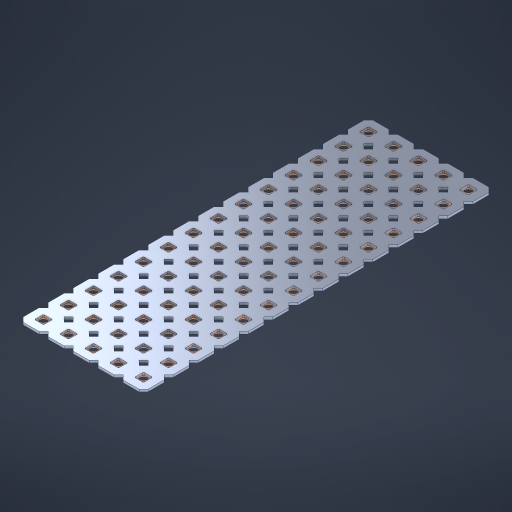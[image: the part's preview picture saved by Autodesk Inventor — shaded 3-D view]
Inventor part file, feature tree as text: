
AUTODESK INVENTOR PART (.ipt)
format: ipt  version: 2023 (Build 270158000, 158)  size: 1,072,128 bytes
history: native  units: in
note: dims shown in document units (in); Inventor stores cm internally (conversion verified against a paired STEP export)
features: other x71, extrude x69, sketch x2, pattern_linear x1
ambient origin geometry x8: Origin, YZ Plane, XZ Plane, XY Plane, X Axis, Y Axis, Z Axis, Center Point
bodies: Solid1 (feature_tree), Body (feature_tree)
feature tree (143):
  pattern_linear  "Rectangular Pattern1"  Spacing1=0.09in  [1 undecoded]
  sketch  "Sketch1"  dims[d1=0.5in]
  sketch  "Sketch2"  dims[d2=0.182in d3=0.09in d4=0.09in d5=0.09in d6=0.09in d7=0.09in d8=0.09in d9=0.09in d10=0.09in d11=0.02in d13=0.0in d14=0.172in d15=0.0625in d16=0.0in d19=0.5in d22=0.5in]
  other  "Srf1"
  other  "Srf126"
  other  "Srf127"
  other  "Srf128"
  other  "Srf129"
  other  "Srf130"
  other  "Srf131"
  other  "Srf250"
  other  "Srf251"
  other  "Srf252"
  other  "Srf253"
  other  "Srf254"
  other  "Srf255"
  other  "Srf256"
  other  "Srf268"
  other  "Srf269"
  other  "Srf270"
  other  "Srf271"
  other  "Srf272"
  other  "Srf273"
  other  "Srf274"
  other  "Srf275"
  other  "Srf276"
  other  "Srf277"
  other  "Srf278"
  other  "Srf279"
  other  "Srf280"
  other  "Srf281"
  other  "Srf293"
  other  "Srf294"
  other  "Srf295"
  other  "Srf296"
  other  "Srf297"
  other  "Srf298"
  other  "Srf299"
  other  "Srf300"
  other  "Srf301"
  other  "Srf302"
  other  "Srf303"
  other  "Srf304"
  other  "Srf305"
  other  "Srf306"
  other  "Srf318"
  other  "Srf319"
  other  "Srf320"
  other  "Srf321"
  other  "Srf322"
  other  "Srf323"
  other  "Srf324"
  other  "Srf325"
  other  "Srf326"
  other  "Srf327"
  other  "Srf328"
  other  "Srf329"
  other  "Srf330"
  other  "Srf331"
  other  "Srf343"
  other  "Srf344"
  other  "Srf345"
  other  "Srf346"
  other  "Srf347"
  other  "Srf348"
  other  "Srf349"
  other  "Srf350"
  other  "Srf351"
  other  "Srf352"
  other  "Srf353"
  other  "Srf354"
  other  "Srf355"
  other  "Srf356"
  other  "Circle"
  extrude  "ExtrusionSrf126"  Depth=0.09in
  extrude  "ExtrusionSrf127"  Depth=0.09in
  extrude  "ExtrusionSrf128"  Depth=0.09in
  extrude  "ExtrusionSrf129"  Depth=0.09in
  extrude  "ExtrusionSrf130"  Depth=0.09in
  extrude  "ExtrusionSrf131"  Depth=0.09in
  extrude  "ExtrusionSrf250"  Depth=0.09in
  extrude  "ExtrusionSrf251"  Depth=0.02in
  extrude  "ExtrusionSrf252"  TaperAngle=0.0deg  [1 undecoded]
  extrude  "ExtrusionSrf253"  Depth=0.5in
  extrude  "ExtrusionSrf254"  Depth=0.5in TaperAngle=0.0deg
  extrude  "ExtrusionSrf255"  Depth=0.5in
  extrude  "ExtrusionSrf256"  Depth=0.5in
  extrude  "ExtrusionSrf268"  [1 undecoded]
  extrude  "ExtrusionSrf269"  [1 undecoded]
  extrude  "ExtrusionSrf270"  [1 undecoded]
  extrude  "ExtrusionSrf271"  [1 undecoded]
  extrude  "ExtrusionSrf272"  [1 undecoded]
  extrude  "ExtrusionSrf273"  [1 undecoded]
  extrude  "ExtrusionSrf274"  [1 undecoded]
  extrude  "ExtrusionSrf275"  [1 undecoded]
  extrude  "ExtrusionSrf276"  [1 undecoded]
  extrude  "ExtrusionSrf277"  [1 undecoded]
  extrude  "ExtrusionSrf278"  [1 undecoded]
  extrude  "ExtrusionSrf279"  [1 undecoded]
  extrude  "ExtrusionSrf280"  [1 undecoded]
  extrude  "ExtrusionSrf281"  [1 undecoded]
  extrude  "ExtrusionSrf293"  [1 undecoded]
  extrude  "ExtrusionSrf294"  [1 undecoded]
  extrude  "ExtrusionSrf295"  [1 undecoded]
  extrude  "ExtrusionSrf296"  [1 undecoded]
  extrude  "ExtrusionSrf297"  [1 undecoded]
  extrude  "ExtrusionSrf298"  [1 undecoded]
  extrude  "ExtrusionSrf299"  [1 undecoded]
  extrude  "ExtrusionSrf300"  [1 undecoded]
  extrude  "ExtrusionSrf301"  [1 undecoded]
  extrude  "ExtrusionSrf302"  [1 undecoded]
  extrude  "ExtrusionSrf303"  [1 undecoded]
  extrude  "ExtrusionSrf304"  [1 undecoded]
  extrude  "ExtrusionSrf305"  [1 undecoded]
  extrude  "ExtrusionSrf306"  [1 undecoded]
  extrude  "ExtrusionSrf318"  [1 undecoded]
  extrude  "ExtrusionSrf319"  [1 undecoded]
  extrude  "ExtrusionSrf320"  [1 undecoded]
  extrude  "ExtrusionSrf321"  [1 undecoded]
  extrude  "ExtrusionSrf322"  [1 undecoded]
  extrude  "ExtrusionSrf323"  [1 undecoded]
  extrude  "ExtrusionSrf324"  [1 undecoded]
  extrude  "ExtrusionSrf325"  [1 undecoded]
  extrude  "ExtrusionSrf326"  [1 undecoded]
  extrude  "ExtrusionSrf327"  [1 undecoded]
  extrude  "ExtrusionSrf328"  [1 undecoded]
  extrude  "ExtrusionSrf329"  [1 undecoded]
  extrude  "ExtrusionSrf330"  [1 undecoded]
  extrude  "ExtrusionSrf331"  [1 undecoded]
  extrude  "ExtrusionSrf343"  [1 undecoded]
  extrude  "ExtrusionSrf344"  [1 undecoded]
  extrude  "ExtrusionSrf345"  [1 undecoded]
  extrude  "ExtrusionSrf346"  [1 undecoded]
  extrude  "ExtrusionSrf347"  [1 undecoded]
  extrude  "ExtrusionSrf348"  [1 undecoded]
  extrude  "ExtrusionSrf349"  [1 undecoded]
  extrude  "ExtrusionSrf350"  [1 undecoded]
  extrude  "ExtrusionSrf351"  [1 undecoded]
  extrude  "ExtrusionSrf352"  [1 undecoded]
  extrude  "ExtrusionSrf353"  [1 undecoded]
  extrude  "ExtrusionSrf354"  [1 undecoded]
  extrude  "ExtrusionSrf355"  [1 undecoded]
  extrude  "ExtrusionSrf356"  [1 undecoded]
note: 58 required parameter values undecoded (feature->parameter linkage not recoverable at this tier; creation-order binding heuristic only, values carry confidence <= 0.55)
